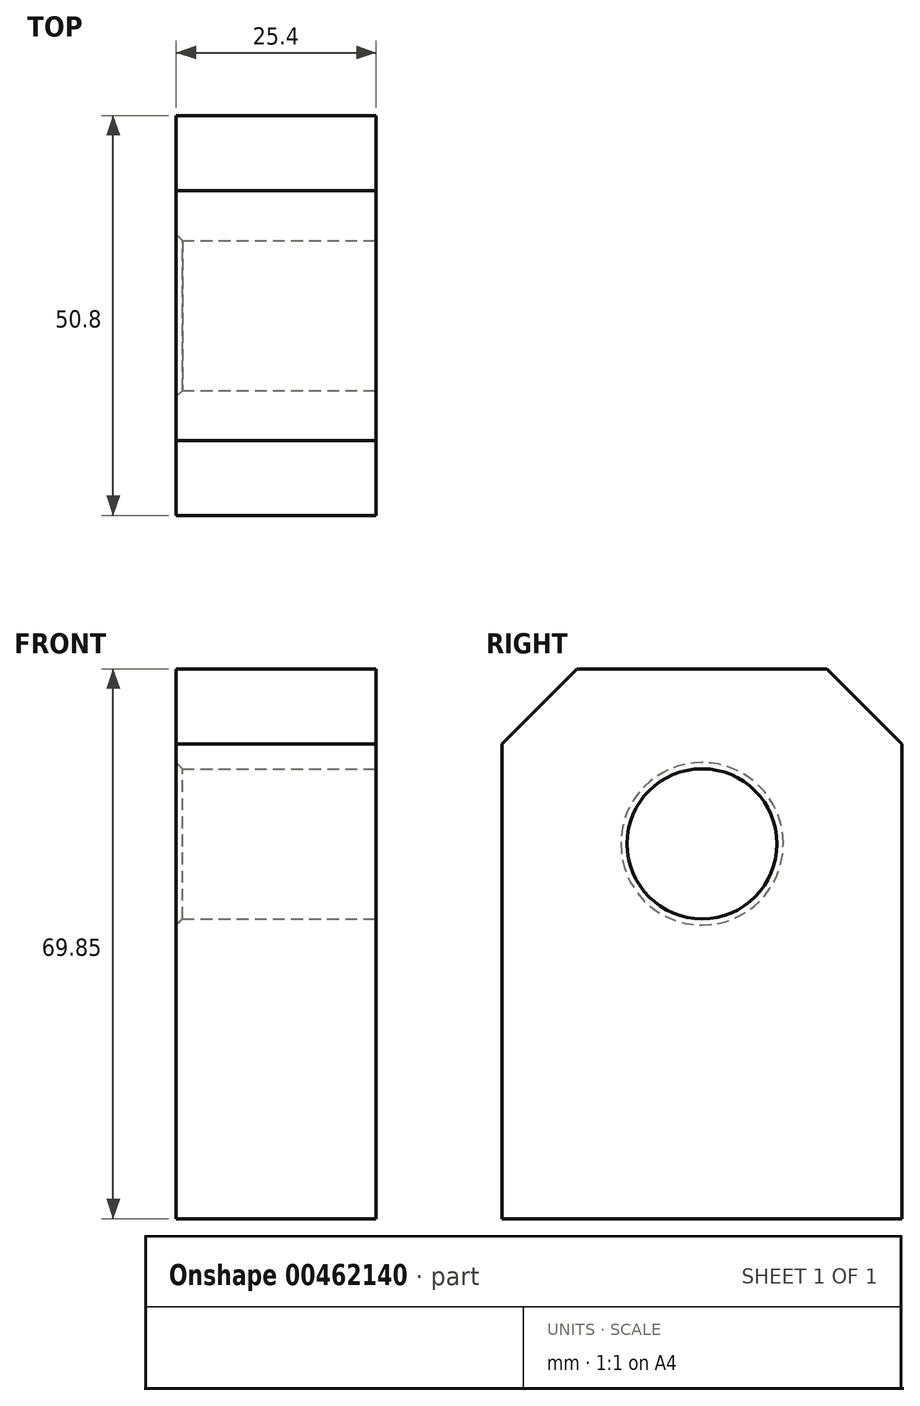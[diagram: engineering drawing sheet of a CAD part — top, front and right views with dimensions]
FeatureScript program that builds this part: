
annotation { "Feature Type Name" : "Feature", "Feature Type Description" : "" }
export const myFeature = defineFeature(function(context is Context, id is Id, definition is map)
    precondition{}
    {
        {
            var Q0;
            Q0=qCreatedBy(makeId("Right.planeOp"),FACE);
            var sketch = newSketch(context, id + "F0", { "sketchPlane" : qUnion([Q0])});
            skLineSegment(sketch, "E0.bottom", {"start": v(0, 0) * mm, "end": v(50.8, 0) * mm});
            skLineSegment(sketch, "E0.top", {"start": v(0, 69.85) * mm, "end": v(50.8, 69.85) * mm});
            skLineSegment(sketch, "E0.left", {"start": v(0, 0) * mm, "end": v(0, 69.85) * mm});
            skLineSegment(sketch, "E0.right", {"start": v(50.8, 0) * mm, "end": v(50.8, 69.85) * mm});
            skSolve(sketch);
        }
        {
            var Q0;
            Q0 = qSketchRegion(id + "F0", true);
            extrude(context, id + "F1", {"entities" : qUnion([Q0]), "depth" : 25.4 * mm});
        }
        {
            var Q0;
            Q0=makeQuery(id+"F1.opExtrude","CAP_FACE",FACE,{"disambiguationData":[OSD([sQuery(id+"F0.wireOp",EDGE,"E0.bottom"),sQuery(id+"F0.wireOp",EDGE,"E0.top"),sQuery(id+"F0.wireOp",EDGE,"E0.left"),sQuery(id+"F0.wireOp",EDGE,"E0.right")])],"isStart":false});
            var sketch = newSketch(context, id + "F2", { "sketchPlane" : qUnion([Q0])});
            skLineSegment(sketch, "E1", {"start": v(25.4, 0) * mm, "end": v(25.4, 69.85) * mm, "construction": true});
            skCircle(sketch, "E2", {"center": v(25.4, 47.62) * mm, "radius": 9.53 * mm});
            skSolve(sketch);
        }
        {
            var Q0;
            Q0 = qSketchRegion(id + "F2", true);
            extrude(context, id + "F3", {"entities" : qUnion([Q0]), "operationType" : NewBodyOperationType.REMOVE, "endBound" : BoundingType.THROUGH_ALL, "oppositeDirection" : true, "depth" : 25.4 * mm});
        }
        {
            var Q0;
            Q0=makeQuery(id+"F1.opExtrude","SWEPT_EDGE",EDGE,{"disambiguationData":[OSD([sQuery(id+"F0.wireOp",EDGE,"E0.top"),sQuery(id+"F0.wireOp",EDGE,"E0.right")])]});
            var Q1;
            Q1=makeQuery(id+"F1.opExtrude","SWEPT_EDGE",EDGE,{"disambiguationData":[OSD([sQuery(id+"F0.wireOp",EDGE,"E0.top"),sQuery(id+"F0.wireOp",EDGE,"E0.left")])]});
            chamfer(context, id + "F4", {"entities" : qUnion([Q0, Q1]), "width" : 9.52 * mm, "tangentPropagation" : true});
        }
        {
            var Q0;
            Q0=makeQuery(id+"F3.boolean.opBoolean","INTERSECT",EDGE,{"derivedFrom":[makeQuery(id+"F1.opExtrude","CAP_FACE",FACE,{"disambiguationData":[OSD([sQuery(id+"F0.wireOp",EDGE,"E0.bottom"),sQuery(id+"F0.wireOp",EDGE,"E0.top"),sQuery(id+"F0.wireOp",EDGE,"E0.left"),sQuery(id+"F0.wireOp",EDGE,"E0.right")])],"isStart":true}),makeQuery(id+"F3.opExtrude","SWEPT_FACE",FACE,{"disambiguationData":[OSD([sQuery(id+"F2.wireOp",EDGE,"E2")])]})]});
            var Q1;
            Q1=makeQuery(id+"F3.boolean.opBoolean","COPY",EDGE,{"derivedFrom":makeQuery(id+"F3.opExtrude","CAP_EDGE",EDGE,{"disambiguationData":[OSD([sQuery(id+"F2.wireOp",EDGE,"E2")])],"isStart":true})});
            chamfer(context, id + "F5", {"entities" : qUnion([Q0, Q1]), "width" : 0.8 * mm, "tangentPropagation" : true});
        }
    });
